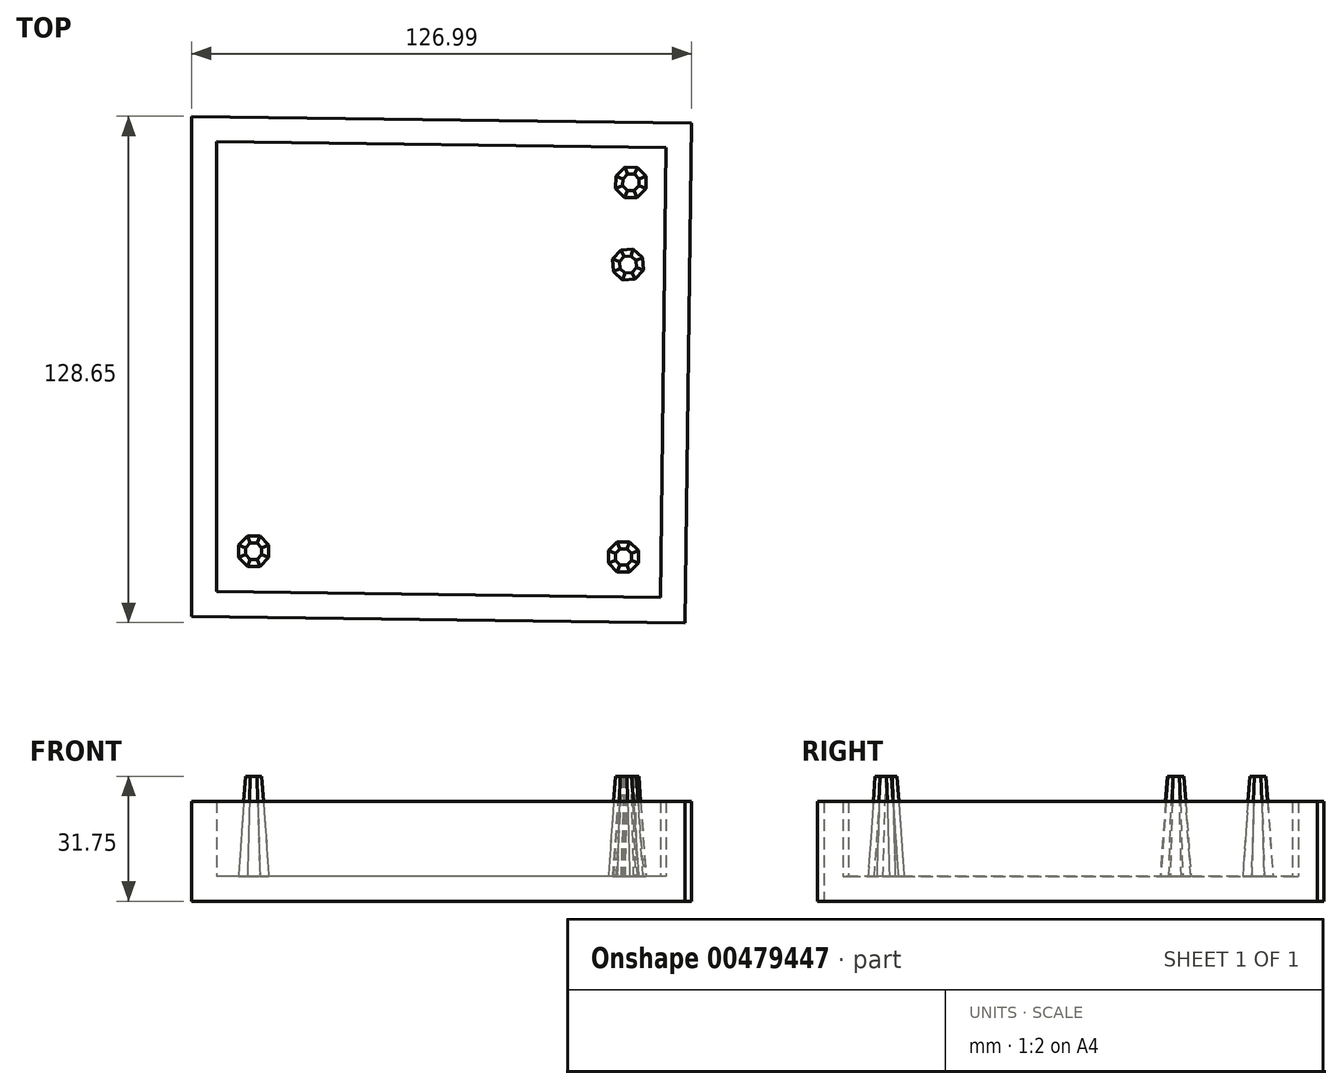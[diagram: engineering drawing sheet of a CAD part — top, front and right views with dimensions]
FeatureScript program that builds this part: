
annotation { "Feature Type Name" : "Feature", "Feature Type Description" : "" }
export const myFeature = defineFeature(function(context is Context, id is Id, definition is map)
    precondition{}
    {
        {
            var Q0;
            Q0=qCreatedBy(makeId("Top.planeOp"),FACE);
            var sketch = newSketch(context, id + "F0", { "sketchPlane" : qUnion([Q0])});
            skLineSegment(sketch, "E0", {"start": v(-50.55, -59.46) * mm, "end": v(-50.55, 67.54) * mm});
            skLineSegment(sketch, "E1", {"start": v(76.44, 65.87) * mm, "end": v(-50.55, 67.54) * mm});
            skLineSegment(sketch, "E2", {"start": v(76.44, 65.87) * mm, "end": v(74.78, -61.11) * mm});
            skLineSegment(sketch, "E3", {"start": v(74.78, -61.11) * mm, "end": v(-50.55, -59.46) * mm});
            skSolve(sketch);
        }
        {
            var Q0;
            Q0 = qSketchRegion(id + "F0", true);
            extrude(context, id + "F1", {"entities" : qUnion([Q0]), "depth" : 25.4 * mm});
        }
        {
            var Q0;
            Q0=makeQuery(id+"F1.opExtrude","CAP_FACE",FACE,{"disambiguationData":[OSD([sQuery(id+"F0.wireOp",EDGE,"E0"),sQuery(id+"F0.wireOp",EDGE,"E1"),sQuery(id+"F0.wireOp",EDGE,"E2"),sQuery(id+"F0.wireOp",EDGE,"E3")])],"isStart":false});
            shell(context, id + "F2", {"entities" : qUnion([Q0]), "thickness" : 6.35 * mm});
        }
        {
            var Q0;
            Q0=makeQuery(id+"F2.opShell","OFFSET_FACE",FACE,{"disambiguationData":[OSD([sQuery(id+"F0.wireOp",EDGE,"E0"),sQuery(id+"F0.wireOp",EDGE,"E1"),sQuery(id+"F0.wireOp",EDGE,"E2"),sQuery(id+"F0.wireOp",EDGE,"E3")])]});
            var sketch = newSketch(context, id + "F3", { "sketchPlane" : qUnion([Q0])});
            skCircle(sketch, "E4.cCircle", {"center": v(61.03, 50.77) * mm, "radius": 3.83 * mm, "construction": true});
            skLineSegment(sketch, "E4.0", {"start": v(57.18, 49.23) * mm, "end": v(57.22, 52.4) * mm});
            skLineSegment(sketch, "E4.1", {"start": v(57.22, 52.4) * mm, "end": v(59.5, 54.62) * mm});
            skLineSegment(sketch, "E4.2", {"start": v(59.5, 54.62) * mm, "end": v(62.67, 54.58) * mm});
            skLineSegment(sketch, "E4.3", {"start": v(62.67, 54.58) * mm, "end": v(64.88, 52.3) * mm});
            skLineSegment(sketch, "E4.4", {"start": v(64.88, 52.3) * mm, "end": v(64.84, 49.13) * mm});
            skLineSegment(sketch, "E4.5", {"start": v(64.84, 49.13) * mm, "end": v(62.57, 46.92) * mm});
            skLineSegment(sketch, "E4.6", {"start": v(62.57, 46.92) * mm, "end": v(59.4, 46.96) * mm});
            skLineSegment(sketch, "E4.7", {"start": v(59.4, 46.96) * mm, "end": v(57.18, 49.23) * mm});
            skPoint(sketch, "E4.0.midPoint", {"position": v(57.2, 50.82) * mm});
            skSolve(sketch);
        }
        {
            var Q0;
            Q0=makeQuery(id+"F3.imprint","IMPRINT",FACE,{"disambiguationData":[TD([[makeQuery(id+"F3.imprint","IMPRINT",EDGE,{"derivedFrom":sQuery(id+"F3.wireOp",EDGE,"E4.0")}),-1.0]])]});
            extrude(context, id + "F4", {"entities" : qUnion([Q0]), "operationType" : NewBodyOperationType.ADD, "depth" : 25.4 * mm, "hasDraft" : true, "draftAngle" : 4 * degree, "draftPullDirection" : true});
        }
        {
            var Q0;
            Q0=makeQuery(id+"F2.opShell","OFFSET_FACE",FACE,{"disambiguationData":[OSD([sQuery(id+"F0.wireOp",EDGE,"E0"),sQuery(id+"F0.wireOp",EDGE,"E1"),sQuery(id+"F0.wireOp",EDGE,"E2"),sQuery(id+"F0.wireOp",EDGE,"E3")])]});
            var sketch = newSketch(context, id + "F5", { "sketchPlane" : qUnion([Q0])});
            skCircle(sketch, "E5.cCircle", {"center": v(-34.8, -42.94) * mm, "radius": 3.83 * mm, "construction": true});
            skLineSegment(sketch, "E5.0", {"start": v(-38.62, -44.53) * mm, "end": v(-38.62, -41.36) * mm});
            skLineSegment(sketch, "E5.1", {"start": v(-38.62, -41.36) * mm, "end": v(-36.38, -39.11) * mm});
            skLineSegment(sketch, "E5.2", {"start": v(-36.38, -39.11) * mm, "end": v(-33.2, -39.11) * mm});
            skLineSegment(sketch, "E5.3", {"start": v(-33.2, -39.11) * mm, "end": v(-30.96, -41.36) * mm});
            skLineSegment(sketch, "E5.4", {"start": v(-30.96, -41.36) * mm, "end": v(-30.96, -44.53) * mm});
            skLineSegment(sketch, "E5.5", {"start": v(-30.96, -44.53) * mm, "end": v(-33.2, -46.78) * mm});
            skLineSegment(sketch, "E5.6", {"start": v(-33.2, -46.78) * mm, "end": v(-36.38, -46.78) * mm});
            skLineSegment(sketch, "E5.7", {"start": v(-36.38, -46.78) * mm, "end": v(-38.62, -44.53) * mm});
            skPoint(sketch, "E5.0.midPoint", {"position": v(-38.62, -42.94) * mm});
            skSolve(sketch);
        }
        {
            var Q0;
            Q0 = qSketchRegion(id + "F5", true);
            extrude(context, id + "F6", {"entities" : qUnion([Q0]), "operationType" : NewBodyOperationType.ADD, "depth" : 25.4 * mm, "hasDraft" : true, "draftAngle" : 4 * degree, "draftPullDirection" : true});
        }
        {
            var Q0;
            Q0=makeQuery(id+"F2.opShell","OFFSET_FACE",FACE,{"disambiguationData":[OSD([sQuery(id+"F0.wireOp",EDGE,"E0"),sQuery(id+"F0.wireOp",EDGE,"E1"),sQuery(id+"F0.wireOp",EDGE,"E2"),sQuery(id+"F0.wireOp",EDGE,"E3")])]});
            var sketch = newSketch(context, id + "F7", { "sketchPlane" : qUnion([Q0])});
            skCircle(sketch, "E6.cCircle", {"center": v(59.16, -44.4) * mm, "radius": 3.83 * mm, "construction": true});
            skLineSegment(sketch, "E6.0", {"start": v(57.58, -40.58) * mm, "end": v(60.75, -40.58) * mm});
            skLineSegment(sketch, "E6.1", {"start": v(60.75, -40.58) * mm, "end": v(63, -42.82) * mm});
            skLineSegment(sketch, "E6.2", {"start": v(63, -42.82) * mm, "end": v(63, -46) * mm});
            skLineSegment(sketch, "E6.3", {"start": v(63, -46) * mm, "end": v(60.75, -48.24) * mm});
            skLineSegment(sketch, "E6.4", {"start": v(60.75, -48.24) * mm, "end": v(57.58, -48.24) * mm});
            skLineSegment(sketch, "E6.5", {"start": v(57.58, -48.24) * mm, "end": v(55.33, -46) * mm});
            skLineSegment(sketch, "E6.6", {"start": v(55.33, -46) * mm, "end": v(55.33, -42.82) * mm});
            skLineSegment(sketch, "E6.7", {"start": v(55.33, -42.82) * mm, "end": v(57.58, -40.58) * mm});
            skPoint(sketch, "E6.0.midPoint", {"position": v(59.16, -40.58) * mm});
            skSolve(sketch);
        }
        {
            var Q0;
            Q0 = qSketchRegion(id + "F7", true);
            extrude(context, id + "F8", {"entities" : qUnion([Q0]), "operationType" : NewBodyOperationType.ADD, "depth" : 25.4 * mm, "hasDraft" : true, "draftAngle" : 4 * degree, "draftPullDirection" : true});
        }
        {
            var Q0;
            Q0=makeQuery(id+"F2.opShell","OFFSET_FACE",FACE,{"disambiguationData":[OSD([sQuery(id+"F0.wireOp",EDGE,"E0"),sQuery(id+"F0.wireOp",EDGE,"E1"),sQuery(id+"F0.wireOp",EDGE,"E2"),sQuery(id+"F0.wireOp",EDGE,"E3")])]});
            var sketch = newSketch(context, id + "F9", { "sketchPlane" : qUnion([Q0])});
            skCircle(sketch, "E7.cCircle", {"center": v(60.3, 29.89) * mm, "radius": 4.15 * mm, "construction": true});
            skLineSegment(sketch, "E7.0", {"start": v(61.65, 33.81) * mm, "end": v(64.03, 31.71) * mm});
            skLineSegment(sketch, "E7.1", {"start": v(64.03, 31.71) * mm, "end": v(64.24, 28.55) * mm});
            skLineSegment(sketch, "E7.2", {"start": v(64.24, 28.55) * mm, "end": v(62.14, 26.16) * mm});
            skLineSegment(sketch, "E7.3", {"start": v(62.14, 26.16) * mm, "end": v(58.97, 25.96) * mm});
            skLineSegment(sketch, "E7.4", {"start": v(58.97, 25.96) * mm, "end": v(56.59, 28.06) * mm});
            skLineSegment(sketch, "E7.5", {"start": v(56.59, 28.06) * mm, "end": v(56.38, 31.22) * mm});
            skLineSegment(sketch, "E7.6", {"start": v(56.38, 31.22) * mm, "end": v(58.48, 33.6) * mm});
            skLineSegment(sketch, "E7.7", {"start": v(58.48, 33.6) * mm, "end": v(61.65, 33.81) * mm});
            skSolve(sketch);
        }
        {
            var Q0;
            Q0 = qSketchRegion(id + "F9", true);
            extrude(context, id + "F10", {"entities" : qUnion([Q0]), "operationType" : NewBodyOperationType.ADD, "depth" : 25.4 * mm, "hasDraft" : true, "draftAngle" : 4 * degree, "draftPullDirection" : true});
        }
    });
